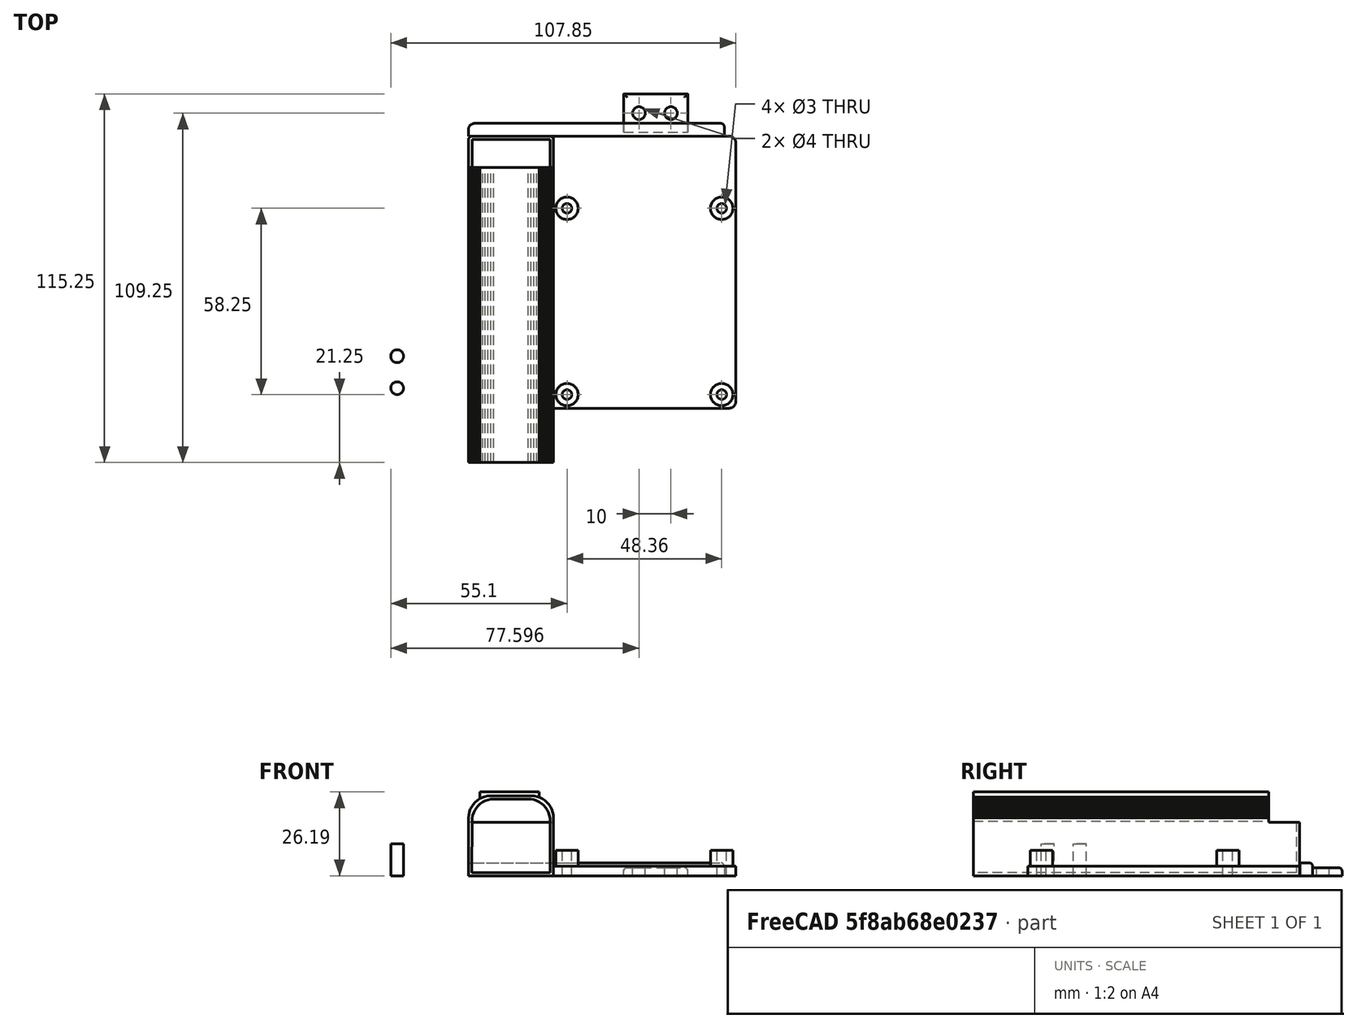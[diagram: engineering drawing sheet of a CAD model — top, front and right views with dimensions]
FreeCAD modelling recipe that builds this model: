
FCSTD DOCUMENT  (FreeCAD 0.16RUnknown)
Label: pinocs-piB
License: All rights reserved
LicenseURL: http://en.wikipedia.org/wiki/All_rights_reserved
objects: Part::Cylinder×10, Part::Fillet×7, Part::MultiFuse×6, Part::Box×4, Part::Feature×2, Part::Cut×2
note: 31 computed .brp shape members not serialized (recipe doc carries the construction recipe); baked Part::Feature solids carry a one-line shape summary decoded from their .brp

FEATURE [Part::Feature] batt_pack_case001_solid001  label="batt_pack_case"
  shape: bbox 26.5 x 102 x 25 mm, 63 faces (baked)
FEATURE [Part::Cylinder] Cylinder  label="block_hole1"
  Angle = 360
  Height = 10
  Radius = 2
FEATURE [Part::Cylinder] Cylinder001  label="block_hole2"
  Angle = 360
  Height = 10
  Placement = pos=(0,10,0) rot=(0,0,1;0rad)
  Radius = 2
FEATURE [Part::MultiFuse] Fusion  label="block_holes_c"
  Shapes = -> [Cylinder,Cylinder001]
FEATURE [Part::Feature] Fusion001  label="block_holes_r"
  Placement = pos=(85.5959,86,-3.74407) rot=(0,0,1;1.5708rad)
  shape: bbox 14 x 4 x 10 mm, 6 faces, 2 solids (baked)
FEATURE [Part::Box] Box  label="Cube"
  Height = 3
  Length = 57
  Placement = pos=(48.85,-6.25,0) rot=(0,0,1;0rad)
  Width = 85
FEATURE [Part::Fillet] Fillet  label="piB+_plate_c"
  Base = -> Box
  Edges = 2 edges r=2: [Edge5,Edge7]
FEATURE [Part::Box] Box001  label="block_attachment"
  Height = 2.5
  Length = 20
  Placement = pos=(70.8495,80,-4.33601e-05) rot=(0,0,1;0rad)
  Width = 12
FEATURE [Part::Box] Box002  label="reinforcement"
  Height = 4
  Length = 80
  Placement = pos=(22.25,78.7903,0) rot=(0,0,1;0rad)
  Width = 4
FEATURE [Part::Fillet] Fillet001
  Base = -> Box002
  Edges = 1 edges r=2: [Edge3]
FEATURE [Part::Fillet] Fillet002
  Base = -> Fillet001
  Edges = 1 edges r=1: [Edge7]
FEATURE [Part::Fillet] Fillet003
  Base = -> batt_pack_case001_solid001
  Edges = 1 edges r=1: [Edge126]
FEATURE [Part::Fillet] Fillet004  label="batt_case_fillet"
  Base = -> Fillet003
  Edges = 1 edges r=1: [Edge12]
FEATURE [Part::Fillet] Fillet005  label="block_attachment_fillet"
  Base = -> Box001
  Edges = 4 edges r=1: [Edge2,Edge6,Edge10,Edge12]
FEATURE [Part::Fillet] Fillet006  label="reinforcement_fillet"
  Base = -> Fillet002
  Edges = 1 edges r=1: [Edge20]
FEATURE [Part::MultiFuse] Fusion002  label="piB-plate-with-batt-blank"
  Shapes = -> [Fillet005,Fillet006,Fillet,Fillet004]
FEATURE [Part::Cut] Cut  label="piB-plate-with-batt-blank_full_c"
  Base = -> Fusion002
  Tool = -> Fusion001
FEATURE [Part::Cylinder] Cylinder002  label="bolt_shoulder1"
  Angle = 360
  Height = 8
  Placement = pos=(53.1,-2,0) rot=(0,0,1;0rad)
  Radius = 3.5
FEATURE [Part::Cylinder] Cylinder003  label="bolt_hole1"
  Angle = 360
  Height = 20
  Placement = pos=(53.1,-2,-1.21245) rot=(0,0,1;0rad)
  Radius = 1.5
  expr: Placement.Base.x = 50.85 + 2.25
FEATURE [Part::Cylinder] Cylinder004  label="bolt_hole002"
  Angle = 360
  Height = 20
  Placement = pos=(101.46,-2,-1.21245) rot=(0,0,1;0rad)
  Radius = 1.5
  expr: Placement.Base.x = 50.85 + 2.25 + 48.36
FEATURE [Part::Cylinder] Cylinder005  label="bolt_shoulder002"
  Angle = 360
  Height = 8
  Placement = pos=(101.46,-2,0) rot=(0,0,1;0rad)
  Radius = 3.5
FEATURE [Part::Cylinder] Cylinder006  label="bolt_hole003"
  Angle = 360
  Height = 20
  Placement = pos=(53.1,56.25,-1.21245) rot=(0,0,1;0rad)
  Radius = 1.5
  expr: Placement.Base.x = 50.85 + 2.25
FEATURE [Part::Cylinder] Cylinder007  label="bolt_shoulder003"
  Angle = 360
  Height = 8
  Placement = pos=(53.1,56.25,0) rot=(0,0,1;0rad)
  Radius = 3.5
FEATURE [Part::Cylinder] Cylinder008  label="bolt_hole004"
  Angle = 360
  Height = 20
  Placement = pos=(101.46,56.25,-1.21245) rot=(0,0,1;0rad)
  Radius = 1.5
  expr: Placement.Base.x = 50.85 + 2.25 + 48.36
FEATURE [Part::Cylinder] Cylinder009  label="bolt_shoulder004"
  Angle = 360
  Height = 8
  Placement = pos=(101.46,56.25,0) rot=(0,0,1;0rad)
  Radius = 3.5
FEATURE [Part::MultiFuse] Fusion003  label="bolt_shoulders_c"
  Shapes = -> [Cylinder009,Cylinder007,Cylinder005,Cylinder002]
FEATURE [Part::MultiFuse] Fusion004  label="bolt_holes_c"
  Shapes = -> [Cylinder003,Cylinder006,Cylinder008,Cylinder004]
FEATURE [Part::MultiFuse] Fusion005  label="full_plate_c"
  Shapes = -> [Cut,Fusion003]
FEATURE [Part::Cut] Cut001  label="full_plate_with_holes_c"
  Base = -> Fusion005
  Tool = -> Fusion004
FEATURE [Part::Box] Box003  label="Cube001"
  Height = 2
  Length = 18.5
  Placement = pos=(25.8995,-23.2251,24.1912) rot=(0,0,1;0rad)
  Width = 92.25
FEATURE [Part::MultiFuse] Fusion006  label="patched_full_plate_w_holes_c"
  Shapes = -> [Box003,Cut001]
